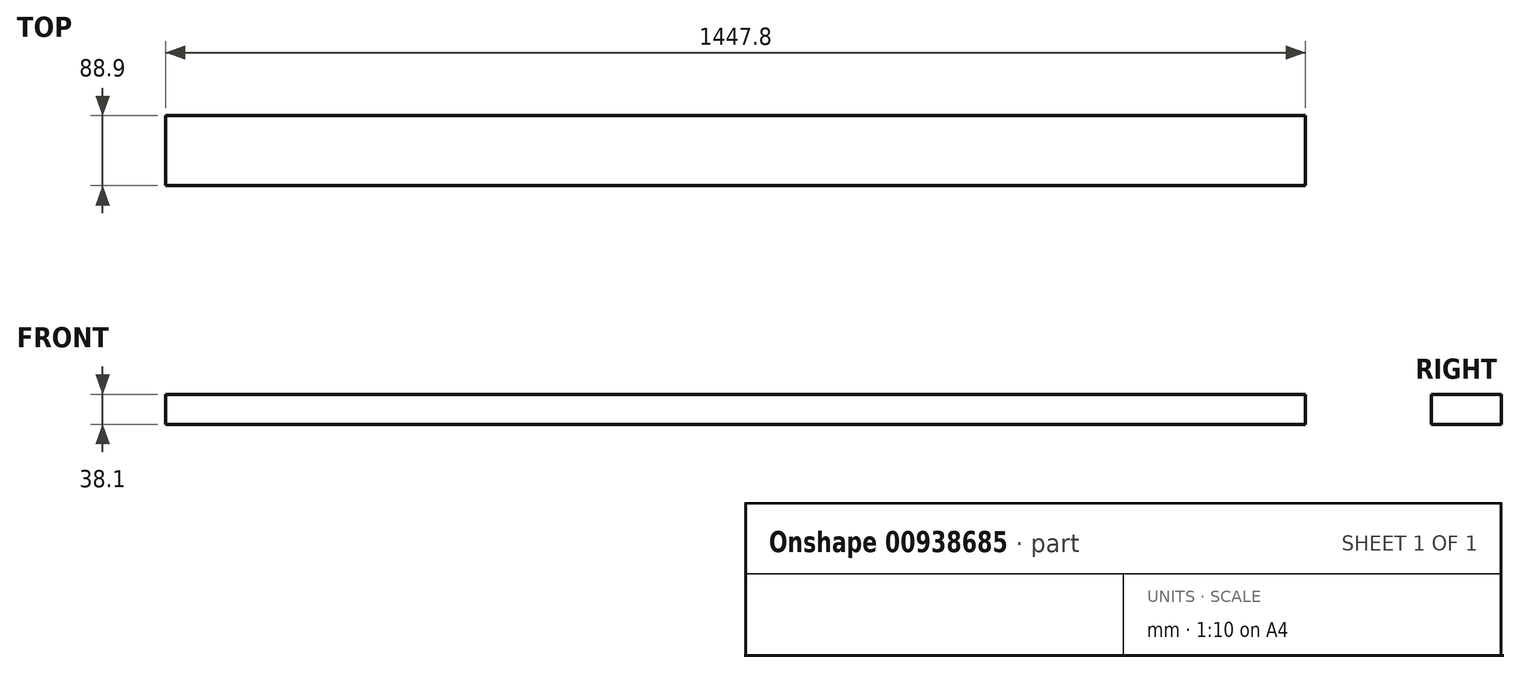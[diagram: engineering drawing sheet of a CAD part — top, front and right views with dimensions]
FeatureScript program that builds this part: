
annotation { "Feature Type Name" : "Feature", "Feature Type Description" : "" }
export const myFeature = defineFeature(function(context is Context, id is Id, definition is map)
    precondition{}
    {
        {
            var Q0;
            Q0=qCreatedBy(makeId("Right.planeOp"),FACE);
            var sketch = newSketch(context, id + "F0", { "sketchPlane" : qUnion([Q0])});
            skLineSegment(sketch, "E0.bottom", {"start": v(44.45, -19.05) * mm, "end": v(-44.45, -19.05) * mm});
            skLineSegment(sketch, "E0.top", {"start": v(44.45, 19.05) * mm, "end": v(-44.45, 19.05) * mm});
            skLineSegment(sketch, "E0.left", {"start": v(44.45, -19.05) * mm, "end": v(44.45, 19.05) * mm});
            skLineSegment(sketch, "E0.right", {"start": v(-44.45, -19.05) * mm, "end": v(-44.45, 19.05) * mm});
            skPoint(sketch, "E0.middle", {"position": v(0, 0) * mm});
            skSolve(sketch);
        }
        {
            var Q0;
            Q0=qSketchRegion(id+"F0",true);
            var Q1;
            Q1=makeQuery(id+"F0.imprint","IMPRINT",FACE,{"disambiguationData":[TD([[makeQuery(id+"F0.imprint","IMPRINT",EDGE,{"derivedFrom":sQuery(id+"F0.wireOp",EDGE,"E0.bottom")}),-1.0]])]});
            extrude(context, id + "F1", {"entities" : qUnion([Q0, Q1]), "depth" : 1447.8 * mm, "offsetDistance" : 25.4 * mm});
        }
    });
